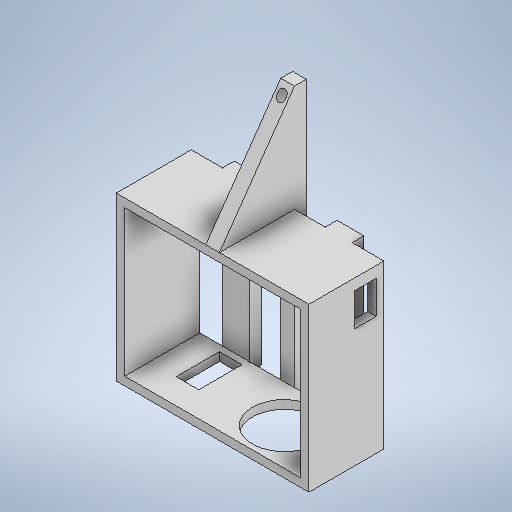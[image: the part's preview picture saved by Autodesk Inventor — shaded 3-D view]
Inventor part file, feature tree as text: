
AUTODESK INVENTOR PART (.ipt)
format: ipt  version: 2025 (Build 290162010, 162A)  size: 357,376 bytes
history: native  units: mm
features: sketch x7, extrude x6, hole x1
ambient origin geometry x8: Origin, YZ Plane, XZ Plane, XY Plane, X Axis, Y Axis, Z Axis, Center Point
bodies: Solid1 (feature_tree)
feature tree (14):
  extrude  "Extrusion1"  Depth=2.5mm
  extrude  "Extrusion3"  Depth=28.65mm
  extrude  "Extrusion4"  Depth=4.064mm
  extrude  "Extrusion5"  Depth=31.75mm TaperAngle=0.0deg
  hole  "Hole3"  [1 undecoded]
  extrude  "Extrusion7"  Depth=3.3mm
  extrude  "Extrusion8"  Depth=20.0mm TaperAngle=0.0deg
  sketch  "Sketch1"  dims[d1=43.42mm d2=2.5mm]
  sketch  "Sketch4"  dims[d3=22.3mm d4=0.0mm d21=28.65mm]
  sketch  "Sketch6"  dims[d22=26.15mm d23=4.064mm]
  sketch  "Sketch7"  dims[d24=7.0mm d25=31.75mm d26=48.42mm d27=0.0mm d28=0.0mm]
  sketch  "Sketch8"  dims[d38=6.4mm d39=9.8mm]
  sketch  "Sketch10"  dims[d40=2.3mm d41=3.3mm]
  sketch  "Sketch12"  dims[d42=20.0mm d43=0.0mm d44=20.0mm d45=0.0mm d46=2.5mm d47=2.032mm d48=2.6416mm d49=7.01mm d50=4.0mm d51=2.0mm d52=90.0deg d53=10.979mm d54=0.0mm d55=77.3mm d59=18.3mm d60=11.3mm d61=19.0mm d62=6.7mm d63=12.9mm d64=40.294mm d65=1.9mm d66=31.75mm d67=0.0mm d69=8.0mm d70=3.5mm d71=3.5mm d72=9.155mm d73=9.155mm d74=31.75mm d75=0.0mm]
note: 1 required parameter value undecoded (feature->parameter linkage not recoverable at this tier; creation-order binding heuristic only, values carry confidence <= 0.55)
